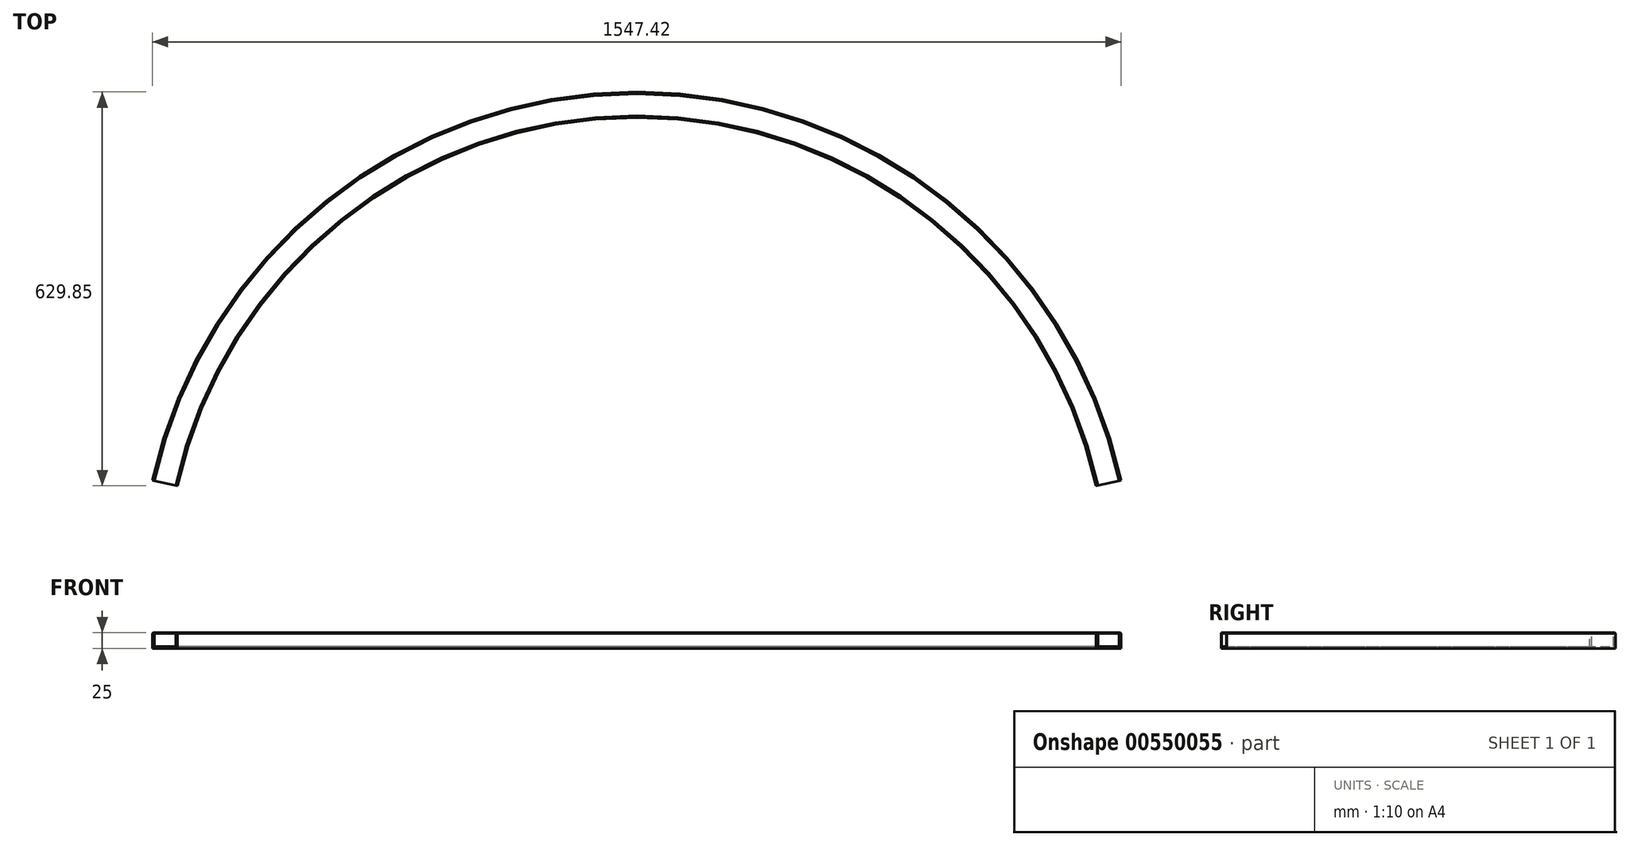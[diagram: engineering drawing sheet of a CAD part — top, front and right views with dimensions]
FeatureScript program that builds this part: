
annotation { "Feature Type Name" : "Feature", "Feature Type Description" : "" }
export const myFeature = defineFeature(function(context is Context, id is Id, definition is map)
    precondition{}
    {
        {
            var Q0;
            Q0=qCreatedBy(makeId("Top.planeOp"),FACE);
            var sketch = newSketch(context, id + "F0", { "sketchPlane" : qUnion([Q0])});
            skLineSegment(sketch, "E0", {"start": v(0, 0) * mm, "end": v(0, 772) * mm, "construction": true});
            skLineSegment(sketch, "E1", {"start": v(0, 0) * mm, "end": v(-243.68, 732.53) * mm, "construction": true});
            skLineSegment(sketch, "E2", {"start": v(0, 0) * mm, "end": v(-167.1, 753.7) * mm, "construction": true});
            skCircle(sketch, "E3", {"center": v(0, 0) * mm, "radius": 772 * mm, "construction": true});
            skPoint(sketch, "E4", {"position": v(-167.1, 753.7) * mm});
            skPoint(sketch, "E5", {"position": v(-243.68, 732.53) * mm});
            skSolve(sketch);
        }
        {
            var Q0;
            Q0=qCreatedBy(makeId("Right.planeOp"),FACE);
            var sketch = newSketch(context, id + "F1", { "sketchPlane" : qUnion([Q0])});
            skLineSegment(sketch, "E6", {"start": v(772, 0) * mm, "end": v(754.5, 0) * mm, "construction": true});
            skLineSegment(sketch, "E7", {"start": v(772, 0) * mm, "end": v(789.5, 0) * mm, "construction": true});
            skLineSegment(sketch, "E8", {"start": v(772, 0) * mm, "end": v(772, -1.22) * mm, "construction": true});
            skLineSegment(sketch, "E9", {"start": v(772, -1.22) * mm, "end": v(757, -1.22) * mm, "construction": true});
            skLineSegment(sketch, "E10", {"start": v(772, -1.22) * mm, "end": v(787, -1.22) * mm, "construction": true});
            skLineSegment(sketch, "E11", {"start": v(754.5, 0) * mm, "end": v(754.5, -22) * mm});
            skLineSegment(sketch, "E12", {"start": v(754.5, -22) * mm, "end": v(789.5, -22) * mm});
            skLineSegment(sketch, "E13", {"start": v(789.5, -22) * mm, "end": v(789.5, 0) * mm});
            skLineSegment(sketch, "E14", {"start": v(754.5, 0) * mm, "end": v(751.5, 0) * mm});
            skLineSegment(sketch, "E15", {"start": v(751.5, 0) * mm, "end": v(751.5, -25) * mm});
            skLineSegment(sketch, "E16", {"start": v(751.5, -25) * mm, "end": v(792.5, -25) * mm});
            skLineSegment(sketch, "E17", {"start": v(792.5, -25) * mm, "end": v(792.5, 0) * mm});
            skLineSegment(sketch, "E18", {"start": v(792.5, 0) * mm, "end": v(789.5, 0) * mm});
            skLineSegment(sketch, "E19", {"start": v(0, 0) * mm, "end": v(0, -52.88) * mm, "construction": true});
            skSolve(sketch);
        }
        {
            var Q0;
            Q0=makeQuery(id+"F1.imprint","IMPRINT",FACE,{"disambiguationData":[TD([[makeQuery(id+"F1.imprint","IMPRINT",EDGE,{"derivedFrom":sQuery(id+"F1.wireOp",EDGE,"E11")}),-1.0]])]});
            var Q1;
            Q1=sQuery(id+"F1.wireOp",EDGE,"E19");
            revolve(context, id + "F2", {"surfaceOperationType" : NewSurfaceOperationType.NEW, "entities" : qUnion([Q0]), "axis" : qUnion([Q1]), "revolveType" : RevolveType.SYMMETRIC, "angle" : 155 * degree});
        }
        {
            var Q0;
            Q0=makeQuery(id+"F2.opRevolve","SWEPT_EDGE",EDGE,{"disambiguationData":[OSD([sQuery(id+"F1.wireOp",EDGE,"E13"),sQuery(id+"F1.wireOp",EDGE,"E18")])]});
            var Q1;
            Q1=makeQuery(id+"F2.opRevolve","SWEPT_EDGE",EDGE,{"disambiguationData":[OSD([sQuery(id+"F1.wireOp",EDGE,"E17"),sQuery(id+"F1.wireOp",EDGE,"E18")])]});
            var Q2;
            Q2=makeQuery(id+"F2.opRevolve","SWEPT_EDGE",EDGE,{"disambiguationData":[OSD([sQuery(id+"F1.wireOp",EDGE,"E14"),sQuery(id+"F1.wireOp",EDGE,"E15")])]});
            var Q3;
            Q3=makeQuery(id+"F2.opRevolve","SWEPT_EDGE",EDGE,{"disambiguationData":[OSD([sQuery(id+"F1.wireOp",EDGE,"E11"),sQuery(id+"F1.wireOp",EDGE,"E14")])]});
            chamfer(context, id + "F3", {"entities" : qUnion([Q0, Q1, Q2, Q3]), "width" : 1 * mm, "tangentPropagation" : true});
        }
        {
            var Q0;
            Q0=makeQuery(id+"F2.opRevolve","SWEPT_EDGE",EDGE,{"disambiguationData":[OSD([sQuery(id+"F1.wireOp",EDGE,"E12"),sQuery(id+"F1.wireOp",EDGE,"E13")])]});
            var Q1;
            Q1=makeQuery(id+"F2.opRevolve","SWEPT_EDGE",EDGE,{"disambiguationData":[OSD([sQuery(id+"F1.wireOp",EDGE,"E11"),sQuery(id+"F1.wireOp",EDGE,"E12")])]});
            fillet(context, id + "F4", {"entities" : qUnion([Q0, Q1]), "radius" : 1 * mm, "tangentPropagation" : true, "allowEdgeOverflow" : false});
        }
    });
